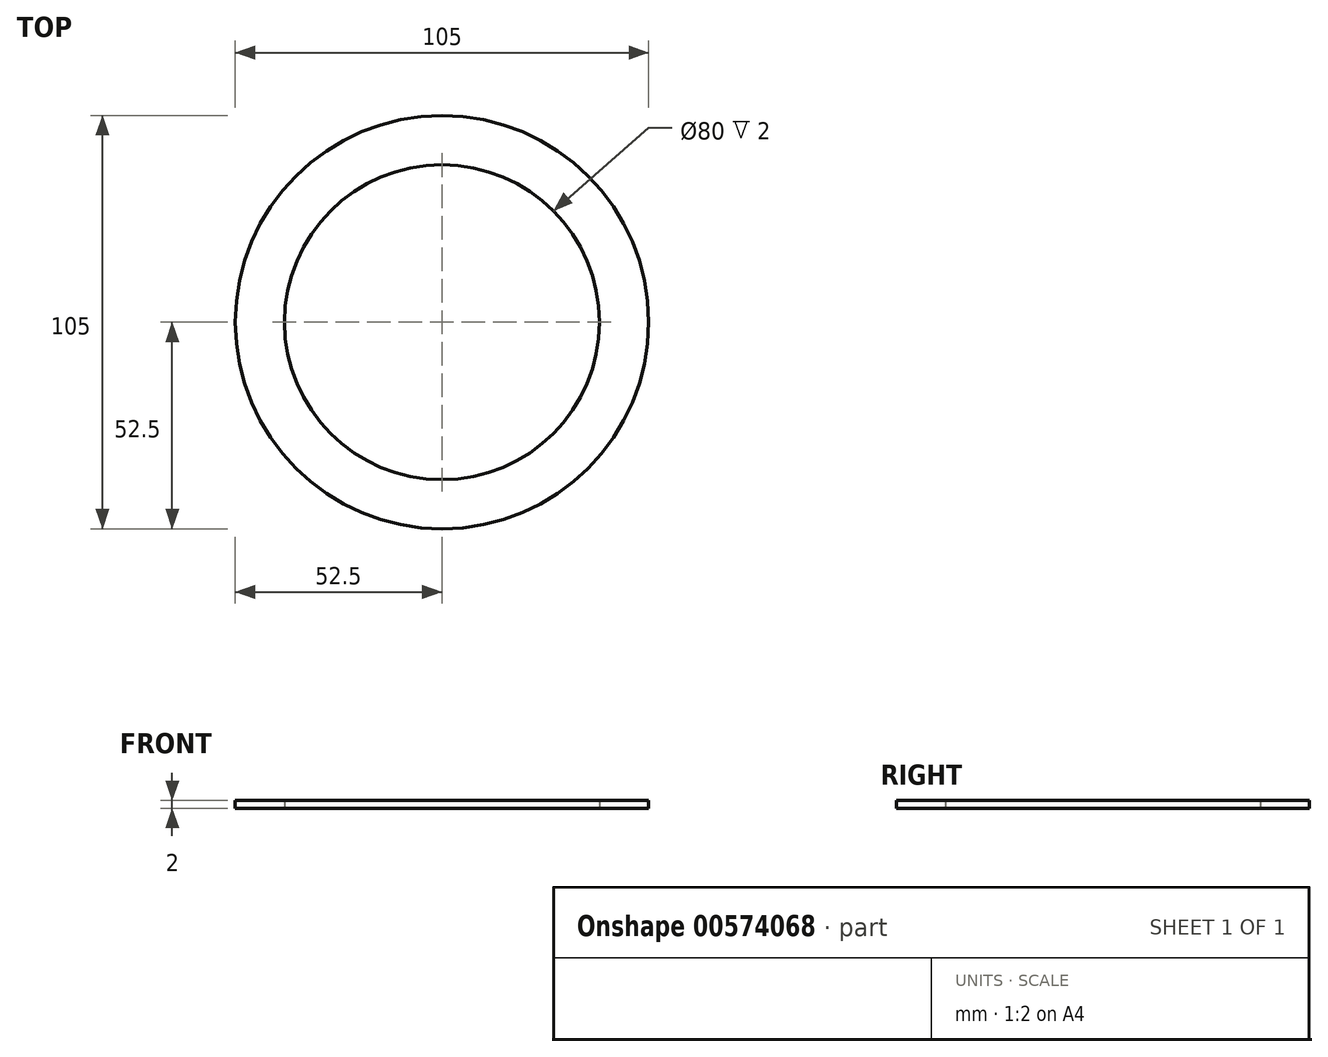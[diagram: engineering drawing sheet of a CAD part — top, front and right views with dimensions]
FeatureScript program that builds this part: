
annotation { "Feature Type Name" : "Feature", "Feature Type Description" : "" }
export const myFeature = defineFeature(function(context is Context, id is Id, definition is map)
    precondition{}
    {
        {
            var Q0;
            Q0=qCreatedBy(makeId("Top.planeOp"),FACE);
            var sketch = newSketch(context, id + "F0", { "sketchPlane" : qUnion([Q0])});
            skCircle(sketch, "E0", {"center": v(0, 0) * mm, "radius": 40 * mm});
            skCircle(sketch, "E1", {"center": v(0, 0) * mm, "radius": 52.5 * mm});
            skSolve(sketch);
        }
        {
            var Q0;
            Q0 = qSketchRegion(id + "F0", true);
            extrude(context, id + "F1", {"entities" : qUnion([Q0]), "depth" : 2 * mm, "offsetDistance" : 25 * mm});
        }
    });
